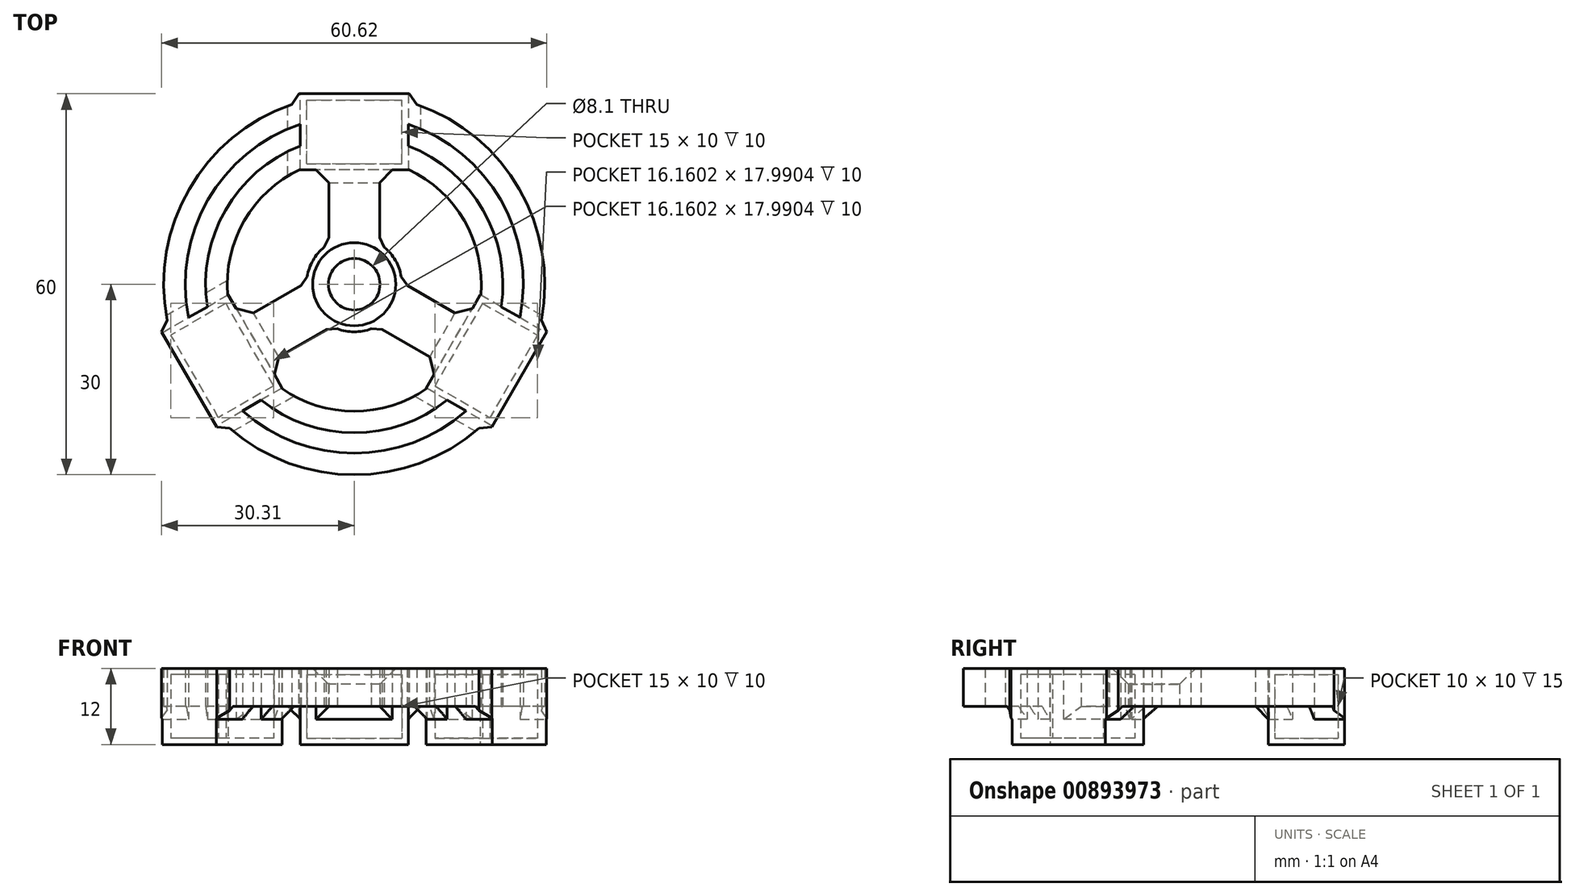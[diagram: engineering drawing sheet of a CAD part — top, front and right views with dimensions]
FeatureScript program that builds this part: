
annotation { "Feature Type Name" : "Feature", "Feature Type Description" : "" }
export const myFeature = defineFeature(function(context is Context, id is Id, definition is map)
    precondition{}
    {
        {
            var Q0;
            Q0=qCreatedBy(makeId("Top.planeOp"),FACE);
            var sketch = newSketch(context, id + "F0", { "sketchPlane" : qUnion([Q0])});
            skCircle(sketch, "E0", {"center": v(0, 0) * mm, "radius": 25 * mm, "construction": true});
            skLineSegment(sketch, "E1", {"start": v(0, 0) * mm, "end": v(0, 40) * mm, "construction": true});
            skLineSegment(sketch, "E2", {"start": v(0, 0) * mm, "end": v(-34.64, -20) * mm, "construction": true});
            skLineSegment(sketch, "E3", {"start": v(0, 0) * mm, "end": v(34.64, -20) * mm, "construction": true});
            skCircle(sketch, "E4", {"center": v(0, 0) * mm, "radius": 4.05 * mm});
            skArc(sketch, "E5", {"start": v(-4, 6.34) * mm, "mid": v(-6.5, 3.75) * mm, "end": v(-7.5, 0.3) * mm});
            skArc(sketch, "E6", {"start": v(-8.5, 28.77) * mm, "mid": v(-25.98, 15) * mm, "end": v(-29.17, -7.02) * mm});
            skCircle(sketch, "E7", {"center": v(0, 0) * mm, "radius": 20 * mm});
            skLineSegment(sketch, "E8.bottom", {"start": v(-8.5, 30) * mm, "end": v(8.5, 30) * mm});
            skLineSegment(sketch, "E8.top", {"start": v(-8.5, 18) * mm, "end": v(-4, 18) * mm});
            skLineSegment(sketch, "E8.left", {"start": v(-8.5, 30) * mm, "end": v(-8.5, 18) * mm});
            skLineSegment(sketch, "E8.right", {"start": v(8.5, 30) * mm, "end": v(8.5, 18) * mm});
            skPoint(sketch, "E9", {"position": v(0, 30) * mm});
            skLineSegment(sketch, "E10.1.0", {"start": v(-21.73, -22.36) * mm, "end": v(-30.23, -7.64) * mm});
            skLineSegment(sketch, "E10.1.1", {"start": v(-30.23, -7.64) * mm, "end": v(-19.84, -1.64) * mm});
            skLineSegment(sketch, "E10.1.2", {"start": v(-11.34, -16.36) * mm, "end": v(-13.59, -12.46) * mm});
            skLineSegment(sketch, "E10.1.3", {"start": v(-21.73, -22.36) * mm, "end": v(-11.34, -16.36) * mm});
            skLineSegment(sketch, "E10.2.0", {"start": v(30.23, -7.64) * mm, "end": v(21.73, -22.36) * mm});
            skLineSegment(sketch, "E10.2.1", {"start": v(21.73, -22.36) * mm, "end": v(11.34, -16.36) * mm});
            skLineSegment(sketch, "E10.2.2", {"start": v(19.84, -1.64) * mm, "end": v(17.59, -5.54) * mm});
            skLineSegment(sketch, "E10.2.3", {"start": v(30.23, -7.64) * mm, "end": v(19.84, -1.64) * mm});
            skArc(sketch, "E11.trimOffspring", {"start": v(-20.67, -21.75) * mm, "mid": v(0, -30) * mm, "end": v(20.67, -21.75) * mm});
            skArc(sketch, "E12.trimOffspring", {"start": v(29.17, -7.02) * mm, "mid": v(25.98, 15) * mm, "end": v(8.5, 28.77) * mm});
            skArc(sketch, "E13", {"start": v(-8.5, 25.2) * mm, "mid": v(-23.04, 13.3) * mm, "end": v(-26.08, -5.24) * mm});
            skArc(sketch, "E14", {"start": v(-8.5, 21.8) * mm, "mid": v(-20.26, 11.7) * mm, "end": v(-23.13, -3.54) * mm});
            skArc(sketch, "E15.trimOffspring", {"start": v(26.08, -5.24) * mm, "mid": v(23.04, 13.3) * mm, "end": v(8.5, 25.2) * mm});
            skArc(sketch, "E16.trimOffspring", {"start": v(23.13, -3.54) * mm, "mid": v(20.26, 11.7) * mm, "end": v(8.5, 21.8) * mm});
            skArc(sketch, "E17.trimOffspring", {"start": v(-17.58, -19.96) * mm, "mid": v(0, -26.6) * mm, "end": v(17.58, -19.96) * mm});
            skArc(sketch, "E18.trimOffspring", {"start": v(-14.63, -18.26) * mm, "mid": v(0, -23.4) * mm, "end": v(14.63, -18.26) * mm});
            skLineSegment(sketch, "E19.left", {"start": v(-4, 18) * mm, "end": v(-4, 6.34) * mm});
            skLineSegment(sketch, "E19.right", {"start": v(4, 18) * mm, "end": v(4, 6.34) * mm});
            skLineSegment(sketch, "E20.trimOffspring", {"start": v(4, 18) * mm, "end": v(8.5, 18) * mm});
            skLineSegment(sketch, "E21.1.0", {"start": v(-13.59, -12.46) * mm, "end": v(-3.5, -6.64) * mm});
            skLineSegment(sketch, "E21.1.1", {"start": v(-17.59, -5.54) * mm, "end": v(-7.5, 0.3) * mm});
            skLineSegment(sketch, "E21.2.0", {"start": v(17.59, -5.54) * mm, "end": v(7.5, 0.3) * mm});
            skLineSegment(sketch, "E21.2.1", {"start": v(13.59, -12.46) * mm, "end": v(3.5, -6.64) * mm});
            skArc(sketch, "E22.trimOffspring", {"start": v(7.5, 0.3) * mm, "mid": v(6.5, 3.75) * mm, "end": v(4, 6.34) * mm});
            skArc(sketch, "E23.trimOffspring", {"start": v(-3.5, -6.64) * mm, "mid": v(0, -7.5) * mm, "end": v(3.5, -6.64) * mm});
            skLineSegment(sketch, "E24.trimOffspring", {"start": v(-17.59, -5.54) * mm, "end": v(-19.84, -1.64) * mm});
            skLineSegment(sketch, "E25.trimOffspring", {"start": v(13.59, -12.46) * mm, "end": v(11.34, -16.36) * mm});
            skSolve(sketch);
        }
        {
            var Q0;
            {var subQ0=sQuery(id+"F0.wireOp",EDGE,"E6");Q0=makeQuery(id+"F0.imprint","IMPRINT",FACE,{"disambiguationData":[TD([[makeQuery(id+"F0.imprint","IMPRINT",EDGE,{"derivedFrom":subQ0}),1.0]])]});}
            var Q1;
            {var subQ3=sQuery(id+"F0.wireOp",EDGE,"E14");Q1=makeQuery(id+"F0.imprint","IMPRINT",FACE,{"disambiguationData":[TD([[makeQuery(id+"F0.imprint","IMPRINT",EDGE,{"derivedFrom":subQ3}),1.0]])]});}
            var Q2;
            {var subQ4=sQuery(id+"F0.wireOp",EDGE,"E8.bottom");Q2=makeQuery(id+"F0.imprint","IMPRINT",FACE,{"disambiguationData":[TD([[makeQuery(id+"F0.imprint","IMPRINT",EDGE,{"derivedFrom":subQ4}),-1.0]])]});}
            var Q3;
            Q3=makeQuery(id+"F0.imprint","IMPRINT",FACE,{"disambiguationData":[TD([[makeQuery(id+"F0.imprint","IMPRINT",EDGE,{"derivedFrom":sQuery(id+"F0.wireOp",EDGE,"E4")}),-1.0]])]});
            var Q4;
            {var subQ14=sQuery(id+"F0.wireOp",EDGE,"E10.1.0");Q4=makeQuery(id+"F0.imprint","IMPRINT",FACE,{"disambiguationData":[TD([[makeQuery(id+"F0.imprint","IMPRINT",EDGE,{"derivedFrom":subQ14}),-1.0]])]});}
            var Q5;
            {var subQ3=sQuery(id+"F0.wireOp",EDGE,"E18.trimOffspring");Q5=makeQuery(id+"F0.imprint","IMPRINT",FACE,{"disambiguationData":[TD([[makeQuery(id+"F0.imprint","IMPRINT",EDGE,{"derivedFrom":subQ3}),1.0]])]});}
            var Q6;
            {var subQ0=sQuery(id+"F0.wireOp",EDGE,"E11.trimOffspring");Q6=makeQuery(id+"F0.imprint","IMPRINT",FACE,{"disambiguationData":[TD([[makeQuery(id+"F0.imprint","IMPRINT",EDGE,{"derivedFrom":subQ0}),1.0]])]});}
            var Q7;
            {var subQ3=sQuery(id+"F0.wireOp",EDGE,"E10.2.0");Q7=makeQuery(id+"F0.imprint","IMPRINT",FACE,{"disambiguationData":[TD([[makeQuery(id+"F0.imprint","IMPRINT",EDGE,{"derivedFrom":subQ3}),-1.0]])]});}
            var Q8;
            {var subQ3=sQuery(id+"F0.wireOp",EDGE,"E16.trimOffspring");Q8=makeQuery(id+"F0.imprint","IMPRINT",FACE,{"disambiguationData":[TD([[makeQuery(id+"F0.imprint","IMPRINT",EDGE,{"derivedFrom":subQ3}),1.0]])]});}
            var Q9;
            {var subQ0=sQuery(id+"F0.wireOp",EDGE,"E12.trimOffspring");Q9=makeQuery(id+"F0.imprint","IMPRINT",FACE,{"disambiguationData":[TD([[makeQuery(id+"F0.imprint","IMPRINT",EDGE,{"derivedFrom":subQ0}),1.0]])]});}
            extrude(context, id + "F1", {"entities" : qUnion([Q0, Q1, Q2, Q3, Q4, Q5, Q6, Q7, Q8, Q9]), "depth" : 6 * mm, "offsetDistance" : 25 * mm});
        }
        {
            var Q0;
            {var subQ4=sQuery(id+"F0.wireOp",EDGE,"E8.bottom");Q0=makeQuery(id+"F0.imprint","IMPRINT",FACE,{"disambiguationData":[TD([[makeQuery(id+"F0.imprint","IMPRINT",EDGE,{"derivedFrom":subQ4}),-1.0]])]});}
            var sketch = newSketch(context, id + "F2", { "sketchPlane" : qUnion([Q0])});
            skLineSegment(sketch, "E26.bottom", {"start": v(8.5, 30) * mm, "end": v(-8.5, 30) * mm});
            skLineSegment(sketch, "E26.top", {"start": v(8.5, 18) * mm, "end": v(-8.5, 18) * mm});
            skLineSegment(sketch, "E26.left", {"start": v(8.5, 30) * mm, "end": v(8.5, 18) * mm});
            skLineSegment(sketch, "E26.right", {"start": v(-8.5, 30) * mm, "end": v(-8.5, 18) * mm});
            skLineSegment(sketch, "E27.1.0", {"start": v(-30.23, -7.64) * mm, "end": v(-19.84, -1.64) * mm});
            skLineSegment(sketch, "E27.1.1", {"start": v(-30.23, -7.64) * mm, "end": v(-21.73, -22.36) * mm});
            skLineSegment(sketch, "E27.1.2", {"start": v(-21.73, -22.36) * mm, "end": v(-11.34, -16.36) * mm});
            skLineSegment(sketch, "E27.1.3", {"start": v(-19.84, -1.64) * mm, "end": v(-11.34, -16.36) * mm});
            skLineSegment(sketch, "E27.2.0", {"start": v(21.73, -22.36) * mm, "end": v(11.34, -16.36) * mm});
            skLineSegment(sketch, "E27.2.1", {"start": v(21.73, -22.36) * mm, "end": v(30.23, -7.64) * mm});
            skLineSegment(sketch, "E27.2.2", {"start": v(30.23, -7.64) * mm, "end": v(19.84, -1.64) * mm});
            skLineSegment(sketch, "E27.2.3", {"start": v(11.34, -16.36) * mm, "end": v(19.84, -1.64) * mm});
            skPoint(sketch, "E27.center", {"position": v(0, 0) * mm});
            skSolve(sketch);
        }
        {
            var Q0;
            Q0 = qSketchRegion(id + "F2", true);
            extrude(context, id + "F3", {"entities" : qUnion([Q0]), "operationType" : NewBodyOperationType.ADD, "oppositeDirection" : true, "depth" : 6 * mm, "offsetDistance" : 25 * mm});
        }
        {
            var Q0;
            Q0=makeQuery(id+"F3.opExtrude","CAP_FACE",FACE,{"disambiguationData":[OSD([sQuery(id+"F2.wireOp",EDGE,"E26.bottom"),sQuery(id+"F2.wireOp",EDGE,"E26.top"),sQuery(id+"F2.wireOp",EDGE,"E26.left"),sQuery(id+"F2.wireOp",EDGE,"E26.right")])],"isStart":false});
            cPlane(context, id + "F4", {"entities" : qUnion([Q0]), "cplaneType" : CPlaneType.OFFSET, "offset" : 1 * mm, "oppositeDirection" : true, "width" : 150 * mm, "height" : 150 * mm});
        }
        {
            var Q0;
            Q0=qCreatedBy(id+"F4.planeOp",FACE);
            var sketch = newSketch(context, id + "F5", { "sketchPlane" : qUnion([Q0])});
            skLineSegment(sketch, "E28.bottom", {"start": v(-7.5, -19) * mm, "end": v(7.5, -19) * mm});
            skLineSegment(sketch, "E28.top", {"start": v(-7.5, -29) * mm, "end": v(7.5, -29) * mm});
            skLineSegment(sketch, "E28.left", {"start": v(-7.5, -19) * mm, "end": v(-7.5, -29) * mm});
            skLineSegment(sketch, "E28.right", {"start": v(7.5, -19) * mm, "end": v(7.5, -29) * mm});
            skLineSegment(sketch, "E29.1.0", {"start": v(20.2, 3) * mm, "end": v(28.86, 8) * mm});
            skLineSegment(sketch, "E29.1.1", {"start": v(20.2, 3) * mm, "end": v(12.7, 16) * mm});
            skLineSegment(sketch, "E29.1.2", {"start": v(12.7, 16) * mm, "end": v(21.36, 21) * mm});
            skLineSegment(sketch, "E29.1.3", {"start": v(28.86, 8) * mm, "end": v(21.36, 21) * mm});
            skLineSegment(sketch, "E29.2.0", {"start": v(-12.7, 16) * mm, "end": v(-21.36, 21) * mm});
            skLineSegment(sketch, "E29.2.1", {"start": v(-12.7, 16) * mm, "end": v(-20.2, 3) * mm});
            skLineSegment(sketch, "E29.2.2", {"start": v(-20.2, 3) * mm, "end": v(-28.86, 8) * mm});
            skLineSegment(sketch, "E29.2.3", {"start": v(-21.36, 21) * mm, "end": v(-28.86, 8) * mm});
            skPoint(sketch, "E29.center", {"position": v(0, 0) * mm});
            skSolve(sketch);
        }
        {
            var Q0;
            Q0 = qSketchRegion(id + "F5", true);
            extrude(context, id + "F6", {"entities" : qUnion([Q0]), "operationType" : NewBodyOperationType.REMOVE, "oppositeDirection" : true, "depth" : 10 * mm, "offsetDistance" : 25 * mm});
        }
        {
            var Q0;
            Q0=makeQuery(id+"F1.opExtrude","SWEPT_EDGE",EDGE,{"disambiguationData":[OSD([sQuery(id+"F0.wireOp",EDGE,"E21.2.1"),sQuery(id+"F0.wireOp",EDGE,"E25.trimOffspring")])]});
            var Q1;
            Q1=makeQuery(id+"F1.opExtrude","SWEPT_EDGE",EDGE,{"disambiguationData":[OSD([sQuery(id+"F0.wireOp",EDGE,"E10.2.2"),sQuery(id+"F0.wireOp",EDGE,"E21.2.0")])]});
            var Q2;
            Q2=makeQuery(id+"F1.opExtrude","SWEPT_EDGE",EDGE,{"disambiguationData":[OSD([sQuery(id+"F0.wireOp",EDGE,"E19.right"),sQuery(id+"F0.wireOp",EDGE,"E20.trimOffspring")])]});
            var Q3;
            Q3=makeQuery(id+"F1.opExtrude","SWEPT_EDGE",EDGE,{"disambiguationData":[OSD([sQuery(id+"F0.wireOp",EDGE,"E8.top"),sQuery(id+"F0.wireOp",EDGE,"E19.left")])]});
            var Q4;
            Q4=makeQuery(id+"F1.opExtrude","SWEPT_EDGE",EDGE,{"disambiguationData":[OSD([sQuery(id+"F0.wireOp",EDGE,"E10.1.2"),sQuery(id+"F0.wireOp",EDGE,"E21.1.0")])]});
            var Q5;
            Q5=makeQuery(id+"F1.opExtrude","SWEPT_EDGE",EDGE,{"disambiguationData":[OSD([sQuery(id+"F0.wireOp",EDGE,"E21.1.1"),sQuery(id+"F0.wireOp",EDGE,"E24.trimOffspring")])]});
            var Q6;
            Q6=makeQuery(id+"F3.opExtrude","CAP_EDGE",EDGE,{"disambiguationData":[OSD([sQuery(id+"F2.wireOp",EDGE,"E27.1.3")])],"isStart":true});
            var Q7;
            Q7=makeQuery(id+"F3.opExtrude","CAP_EDGE",EDGE,{"disambiguationData":[OSD([sQuery(id+"F2.wireOp",EDGE,"E26.top")])],"isStart":true});
            var Q8;
            Q8=makeQuery(id+"F3.opExtrude","CAP_EDGE",EDGE,{"disambiguationData":[OSD([sQuery(id+"F2.wireOp",EDGE,"E27.2.3")])],"isStart":true});
            var Q9;
            Q9=makeQuery(id+"F1.opExtrude","SWEPT_EDGE",EDGE,{"disambiguationData":[OSD([sQuery(id+"F0.wireOp",EDGE,"E5"),sQuery(id+"F0.wireOp",EDGE,"E21.1.1")])]});
            var Q10;
            Q10=makeQuery(id+"F1.opExtrude","SWEPT_EDGE",EDGE,{"disambiguationData":[OSD([sQuery(id+"F0.wireOp",EDGE,"E5"),sQuery(id+"F0.wireOp",EDGE,"E19.left")])]});
            var Q11;
            Q11=makeQuery(id+"F1.opExtrude","SWEPT_EDGE",EDGE,{"disambiguationData":[OSD([sQuery(id+"F0.wireOp",EDGE,"E21.2.1"),sQuery(id+"F0.wireOp",EDGE,"E23.trimOffspring")])]});
            var Q12;
            Q12=makeQuery(id+"F1.opExtrude","SWEPT_EDGE",EDGE,{"disambiguationData":[OSD([sQuery(id+"F0.wireOp",EDGE,"E21.1.0"),sQuery(id+"F0.wireOp",EDGE,"E23.trimOffspring")])]});
            var Q13;
            Q13=makeQuery(id+"F1.opExtrude","SWEPT_EDGE",EDGE,{"disambiguationData":[OSD([sQuery(id+"F0.wireOp",EDGE,"E19.right"),sQuery(id+"F0.wireOp",EDGE,"E22.trimOffspring")])]});
            var Q14;
            Q14=makeQuery(id+"F1.opExtrude","SWEPT_EDGE",EDGE,{"disambiguationData":[OSD([sQuery(id+"F0.wireOp",EDGE,"E21.2.0"),sQuery(id+"F0.wireOp",EDGE,"E22.trimOffspring")])]});
            var Q15;
            Q15=makeQuery(id+"F1.opExtrude","SWEPT_EDGE",EDGE,{"disambiguationData":[OSD([sQuery(id+"F0.wireOp",EDGE,"E10.2.3"),sQuery(id+"F0.wireOp",EDGE,"E12.trimOffspring")])]});
            var Q16;
            Q16=makeQuery(id+"F1.opExtrude","SWEPT_EDGE",EDGE,{"disambiguationData":[OSD([sQuery(id+"F0.wireOp",EDGE,"E8.right"),sQuery(id+"F0.wireOp",EDGE,"E12.trimOffspring")])]});
            var Q17;
            {var subQ6=sQuery(id+"F0.wireOp",EDGE,"E12.trimOffspring");var subQ7=sQuery(id+"F2.wireOp",EDGE,"E26.left");Q17=makeQuery(id+"F3.boolean.opBoolean","SPLIT",EDGE,{"disambiguationData":[TD([makeQuery(id+"F1.opExtrude","SWEPT_FACE",FACE,{"disambiguationData":[OSD([subQ6])]})])],"derivedFrom":makeQuery(id+"F3.opExtrude","CAP_EDGE",EDGE,{"disambiguationData":[OSD([subQ7])],"isStart":true})});}
            var Q18;
            {var subQ2=sQuery(id+"F0.wireOp",EDGE,"E16.trimOffspring");var subQ9=sQuery(id+"F2.wireOp",EDGE,"E26.left");Q18=makeQuery(id+"F3.boolean.opBoolean","SPLIT",EDGE,{"disambiguationData":[TD([makeQuery(id+"F1.opExtrude","SWEPT_FACE",FACE,{"disambiguationData":[OSD([subQ2])]})])],"derivedFrom":makeQuery(id+"F3.opExtrude","CAP_EDGE",EDGE,{"disambiguationData":[OSD([subQ9])],"isStart":true})});}
            var Q19;
            {var subQ2=sQuery(id+"F0.wireOp",EDGE,"E16.trimOffspring");var subQ9=sQuery(id+"F2.wireOp",EDGE,"E27.2.2");Q19=makeQuery(id+"F3.boolean.opBoolean","SPLIT",EDGE,{"disambiguationData":[TD([makeQuery(id+"F1.opExtrude","SWEPT_FACE",FACE,{"disambiguationData":[OSD([subQ2])]})])],"derivedFrom":makeQuery(id+"F3.opExtrude","CAP_EDGE",EDGE,{"disambiguationData":[OSD([subQ9])],"isStart":true})});}
            var Q20;
            {var subQ4=sQuery(id+"F0.wireOp",EDGE,"E12.trimOffspring");var subQ7=sQuery(id+"F2.wireOp",EDGE,"E27.2.2");Q20=makeQuery(id+"F3.boolean.opBoolean","SPLIT",EDGE,{"disambiguationData":[TD([makeQuery(id+"F1.opExtrude","SWEPT_FACE",FACE,{"disambiguationData":[OSD([subQ4])]})])],"derivedFrom":makeQuery(id+"F3.opExtrude","CAP_EDGE",EDGE,{"disambiguationData":[OSD([subQ7])],"isStart":true})});}
            var Q21;
            Q21=makeQuery(id+"F1.opExtrude","SWEPT_EDGE",EDGE,{"disambiguationData":[OSD([sQuery(id+"F0.wireOp",EDGE,"E10.2.1"),sQuery(id+"F0.wireOp",EDGE,"E11.trimOffspring")])]});
            var Q22;
            {var subQ5=sQuery(id+"F0.wireOp",EDGE,"E11.trimOffspring");var subQ7=sQuery(id+"F2.wireOp",EDGE,"E27.2.0");Q22=makeQuery(id+"F3.boolean.opBoolean","SPLIT",EDGE,{"disambiguationData":[TD([makeQuery(id+"F1.opExtrude","SWEPT_FACE",FACE,{"disambiguationData":[OSD([subQ5])]})])],"derivedFrom":makeQuery(id+"F3.opExtrude","CAP_EDGE",EDGE,{"disambiguationData":[OSD([subQ7])],"isStart":true})});}
            var Q23;
            {var subQ4=sQuery(id+"F0.wireOp",EDGE,"E18.trimOffspring");var subQ8=sQuery(id+"F2.wireOp",EDGE,"E27.2.0");Q23=makeQuery(id+"F3.boolean.opBoolean","SPLIT",EDGE,{"disambiguationData":[TD([makeQuery(id+"F1.opExtrude","SWEPT_FACE",FACE,{"disambiguationData":[OSD([subQ4])]})])],"derivedFrom":makeQuery(id+"F3.opExtrude","CAP_EDGE",EDGE,{"disambiguationData":[OSD([subQ8])],"isStart":true})});}
            var Q24;
            {var subQ2=sQuery(id+"F0.wireOp",EDGE,"E18.trimOffspring");var subQ9=sQuery(id+"F2.wireOp",EDGE,"E27.1.2");Q24=makeQuery(id+"F3.boolean.opBoolean","SPLIT",EDGE,{"disambiguationData":[TD([makeQuery(id+"F1.opExtrude","SWEPT_FACE",FACE,{"disambiguationData":[OSD([subQ2])]})])],"derivedFrom":makeQuery(id+"F3.opExtrude","CAP_EDGE",EDGE,{"disambiguationData":[OSD([subQ9])],"isStart":true})});}
            var Q25;
            {var subQ5=sQuery(id+"F0.wireOp",EDGE,"E11.trimOffspring");var subQ7=sQuery(id+"F2.wireOp",EDGE,"E27.1.2");Q25=makeQuery(id+"F3.boolean.opBoolean","SPLIT",EDGE,{"disambiguationData":[TD([makeQuery(id+"F1.opExtrude","SWEPT_FACE",FACE,{"disambiguationData":[OSD([subQ5])]})])],"derivedFrom":makeQuery(id+"F3.opExtrude","CAP_EDGE",EDGE,{"disambiguationData":[OSD([subQ7])],"isStart":true})});}
            var Q26;
            Q26=makeQuery(id+"F1.opExtrude","SWEPT_EDGE",EDGE,{"disambiguationData":[OSD([sQuery(id+"F0.wireOp",EDGE,"E10.1.3"),sQuery(id+"F0.wireOp",EDGE,"E11.trimOffspring")])]});
            var Q27;
            Q27=makeQuery(id+"F1.opExtrude","SWEPT_EDGE",EDGE,{"disambiguationData":[OSD([sQuery(id+"F0.wireOp",EDGE,"E6"),sQuery(id+"F0.wireOp",EDGE,"E10.1.1")])]});
            var Q28;
            {var subQ3=sQuery(id+"F0.wireOp",EDGE,"E6");var subQ7=sQuery(id+"F2.wireOp",EDGE,"E27.1.0");Q28=makeQuery(id+"F3.boolean.opBoolean","SPLIT",EDGE,{"disambiguationData":[TD([makeQuery(id+"F1.opExtrude","SWEPT_FACE",FACE,{"disambiguationData":[OSD([subQ3])]})])],"derivedFrom":makeQuery(id+"F3.opExtrude","CAP_EDGE",EDGE,{"disambiguationData":[OSD([subQ7])],"isStart":true})});}
            var Q29;
            {var subQ2=sQuery(id+"F0.wireOp",EDGE,"E14");var subQ9=sQuery(id+"F2.wireOp",EDGE,"E27.1.0");Q29=makeQuery(id+"F3.boolean.opBoolean","SPLIT",EDGE,{"disambiguationData":[TD([makeQuery(id+"F1.opExtrude","SWEPT_FACE",FACE,{"disambiguationData":[OSD([subQ2])]})])],"derivedFrom":makeQuery(id+"F3.opExtrude","CAP_EDGE",EDGE,{"disambiguationData":[OSD([subQ9])],"isStart":true})});}
            var Q30;
            Q30=makeQuery(id+"F1.opExtrude","SWEPT_EDGE",EDGE,{"disambiguationData":[OSD([sQuery(id+"F0.wireOp",EDGE,"E6"),sQuery(id+"F0.wireOp",EDGE,"E8.left")])]});
            var Q31;
            {var subQ1=sQuery(id+"F0.wireOp",EDGE,"E6");var subQ3=sQuery(id+"F2.wireOp",EDGE,"E26.right");Q31=makeQuery(id+"F3.boolean.opBoolean","SPLIT",EDGE,{"disambiguationData":[TD([makeQuery(id+"F1.opExtrude","SWEPT_FACE",FACE,{"disambiguationData":[OSD([subQ1])]})])],"derivedFrom":makeQuery(id+"F3.opExtrude","CAP_EDGE",EDGE,{"disambiguationData":[OSD([subQ3])],"isStart":true})});}
            var Q32;
            {var subQ3=sQuery(id+"F2.wireOp",EDGE,"E26.right");var subQ8=sQuery(id+"F0.wireOp",EDGE,"E14");Q32=makeQuery(id+"F3.boolean.opBoolean","SPLIT",EDGE,{"disambiguationData":[TD([makeQuery(id+"F1.opExtrude","SWEPT_FACE",FACE,{"disambiguationData":[OSD([subQ8])]})])],"derivedFrom":makeQuery(id+"F3.opExtrude","CAP_EDGE",EDGE,{"disambiguationData":[OSD([subQ3])],"isStart":true})});}
            chamfer(context, id + "F7", {"entities" : qUnion([Q0, Q1, Q2, Q3, Q4, Q5, Q6, Q7, Q8, Q9, Q10, Q11, Q12, Q13, Q14, Q15, Q16, Q17, Q18, Q19, Q20, Q21, Q22, Q23, Q24, Q25, Q26, Q27, Q28, Q29, Q30, Q31, Q32]), "width" : 2 * mm, "tangentPropagation" : true});
        }
        {
            var Q0;
            Q0=makeQuery(id+"F1.opExtrude","CAP_EDGE",EDGE,{"disambiguationData":[OSD([sQuery(id+"F0.wireOp",EDGE,"E4")])],"isStart":false});
            chamfer(context, id + "F8", {"entities" : qUnion([Q0]), "width" : 2.5 * mm, "tangentPropagation" : true});
        }
    });
